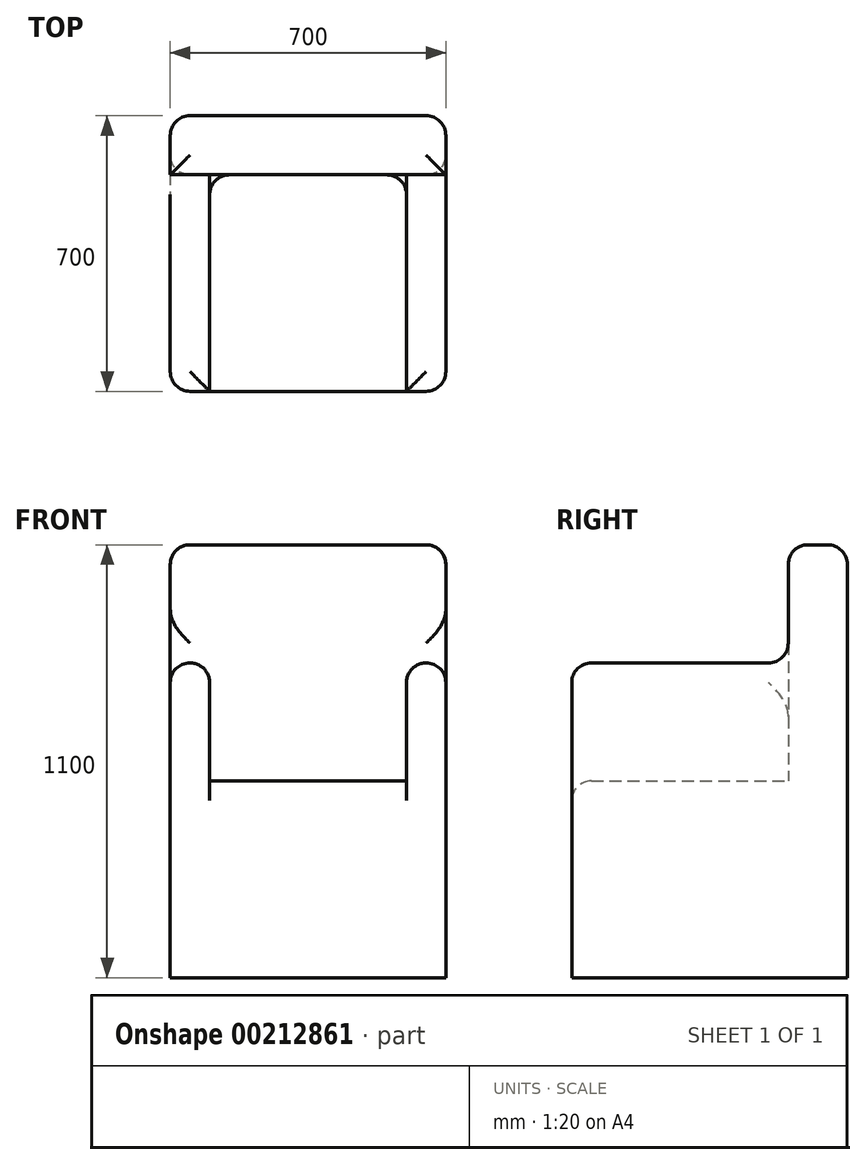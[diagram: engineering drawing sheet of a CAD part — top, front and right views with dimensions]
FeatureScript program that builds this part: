
annotation { "Feature Type Name" : "Feature", "Feature Type Description" : "" }
export const myFeature = defineFeature(function(context is Context, id is Id, definition is map)
    precondition{}
    {
        {
            var Q0;
            Q0=qCreatedBy(makeId("Top.planeOp"),FACE);
            var sketch = newSketch(context, id + "F0", { "sketchPlane" : qUnion([Q0])});
            skLineSegment(sketch, "E0.bottom", {"start": v(0, 0) * mm, "end": v(700, 0) * mm});
            skLineSegment(sketch, "E0.top", {"start": v(0, 700) * mm, "end": v(700, 700) * mm});
            skLineSegment(sketch, "E0.left", {"start": v(0, 0) * mm, "end": v(0, 700) * mm});
            skLineSegment(sketch, "E0.right", {"start": v(700, 0) * mm, "end": v(700, 700) * mm});
            skSolve(sketch);
        }
        {
            var Q0;
            Q0 = qSketchRegion(id + "F0", true);
            extrude(context, id + "F1", {"entities" : qUnion([Q0]), "depth" : 500 * mm});
        }
        {
            var Q0;
            Q0=makeQuery(id+"F1.opExtrude","CAP_FACE",FACE,{"disambiguationData":[OSD([sQuery(id+"F0.wireOp",EDGE,"E0.bottom"),sQuery(id+"F0.wireOp",EDGE,"E0.top"),sQuery(id+"F0.wireOp",EDGE,"E0.left"),sQuery(id+"F0.wireOp",EDGE,"E0.right")])],"isStart":false});
            var sketch = newSketch(context, id + "F2", { "sketchPlane" : qUnion([Q0])});
            skLineSegment(sketch, "E1", {"start": v(0, 0) * mm, "end": v(0, 700) * mm});
            skLineSegment(sketch, "E2", {"start": v(0, 700) * mm, "end": v(700, 700) * mm});
            skLineSegment(sketch, "E3", {"start": v(700, 700) * mm, "end": v(700, 0) * mm});
            skLineSegment(sketch, "E4", {"start": v(700, 0) * mm, "end": v(600, 0) * mm});
            skLineSegment(sketch, "E5", {"start": v(600, 0) * mm, "end": v(600, 550) * mm});
            skLineSegment(sketch, "E6", {"start": v(600, 550) * mm, "end": v(350, 550) * mm});
            skPoint(sketch, "E6.endSnap0", {"position": v(350, 700) * mm});
            skLineSegment(sketch, "E7", {"start": v(350, 700) * mm, "end": v(350, 438.14) * mm, "construction": true});
            skLineSegment(sketch, "E8.MirrorCS", {"start": v(100, 550) * mm, "end": v(350, 550) * mm});
            skLineSegment(sketch, "E9.MirrorCS", {"start": v(100, 0) * mm, "end": v(100, 550) * mm});
            skLineSegment(sketch, "E10.MirrorCS", {"start": v(0, 0) * mm, "end": v(100, 0) * mm});
            skSolve(sketch);
        }
        {
            var Q0;
            Q0 = qSketchRegion(id + "F2", true);
            extrude(context, id + "F3", {"entities" : qUnion([Q0]), "operationType" : NewBodyOperationType.ADD, "depth" : 300 * mm});
        }
        {
            var Q0;
            Q0=makeQuery(id+"F3.opExtrude","CAP_EDGE",EDGE,{"disambiguationData":[OSD([sQuery(id+"F2.wireOp",EDGE,"E6"),sQuery(id+"F2.wireOp",EDGE,"E8.MirrorCS")])],"isStart":true});
            var Q1;
            Q1=makeQuery(id+"F3.opExtrude","CAP_EDGE",EDGE,{"disambiguationData":[OSD([sQuery(id+"F2.wireOp",EDGE,"E5")])],"isStart":true});
            var Q2;
            Q2=makeQuery(id+"F1.opExtrude","CAP_EDGE",EDGE,{"disambiguationData":[OSD([sQuery(id+"F0.wireOp",EDGE,"E0.bottom")])],"isStart":false});
            var Q3;
            Q3=makeQuery(id+"F3.opExtrude","CAP_EDGE",EDGE,{"disambiguationData":[OSD([sQuery(id+"F2.wireOp",EDGE,"E9.MirrorCS")])],"isStart":true});
            var Q4;
            Q4=makeQuery(id+"F3.boolean.opBoolean","MERGE",EDGE,{"derivedFrom":[makeQuery(id+"F1.opExtrude","SWEPT_EDGE",EDGE,{"disambiguationData":[OSD([sQuery(id+"F0.wireOp",EDGE,"E0.bottom"),sQuery(id+"F0.wireOp",EDGE,"E0.right")])]}),makeQuery(id+"F3.opExtrude","SWEPT_EDGE",EDGE,{"disambiguationData":[OSD([sQuery(id+"F2.wireOp",EDGE,"E3"),sQuery(id+"F2.wireOp",EDGE,"E4")])]})]});
            var Q5;
            Q5=makeQuery(id+"F3.boolean.opBoolean","MERGE",EDGE,{"derivedFrom":[makeQuery(id+"F1.opExtrude","SWEPT_EDGE",EDGE,{"disambiguationData":[OSD([sQuery(id+"F0.wireOp",EDGE,"E0.bottom"),sQuery(id+"F0.wireOp",EDGE,"E0.left")])]}),makeQuery(id+"F3.opExtrude","SWEPT_EDGE",EDGE,{"disambiguationData":[OSD([sQuery(id+"F2.wireOp",EDGE,"E1"),sQuery(id+"F2.wireOp",EDGE,"E10.MirrorCS")])]})]});
            fillet(context, id + "F4", {"entities" : qUnion([Q0, Q1, Q2, Q3, Q4, Q5]), "radius" : 50 * mm, "tangentPropagation" : true, "allowEdgeOverflow" : false});
        }
        {
            var Q0;
            Q0=makeQuery(id+"F3.opExtrude","CAP_FACE",FACE,{"disambiguationData":[OSD([sQuery(id+"F2.wireOp",EDGE,"E1"),sQuery(id+"F2.wireOp",EDGE,"E2"),sQuery(id+"F2.wireOp",EDGE,"E3"),sQuery(id+"F2.wireOp",EDGE,"E4"),sQuery(id+"F2.wireOp",EDGE,"E5"),sQuery(id+"F2.wireOp",EDGE,"E6"),sQuery(id+"F2.wireOp",EDGE,"E8.MirrorCS"),sQuery(id+"F2.wireOp",EDGE,"E9.MirrorCS"),sQuery(id+"F2.wireOp",EDGE,"E10.MirrorCS")])],"isStart":false});
            var sketch = newSketch(context, id + "F5", { "sketchPlane" : qUnion([Q0])});
            skLineSegment(sketch, "E11.bottom", {"start": v(0, 700) * mm, "end": v(700, 700) * mm});
            skLineSegment(sketch, "E11.top", {"start": v(0, 550) * mm, "end": v(700, 550) * mm});
            skLineSegment(sketch, "E11.left", {"start": v(0, 700) * mm, "end": v(0, 550) * mm});
            skLineSegment(sketch, "E11.right", {"start": v(700, 700) * mm, "end": v(700, 550) * mm});
            skSolve(sketch);
        }
        {
            var Q0;
            Q0 = qSketchRegion(id + "F5", true);
            extrude(context, id + "F6", {"entities" : qUnion([Q0]), "operationType" : NewBodyOperationType.ADD, "depth" : 300 * mm});
        }
        {
            var Q0;
            Q0=makeQuery(id+"F6.opExtrude","CAP_FACE",FACE,{"disambiguationData":[OSD([sQuery(id+"F5.wireOp",EDGE,"E11.bottom"),sQuery(id+"F5.wireOp",EDGE,"E11.top"),sQuery(id+"F5.wireOp",EDGE,"E11.left"),sQuery(id+"F5.wireOp",EDGE,"E11.right")])],"isStart":false});
            var Q1;
            {var subQ0=sQuery(id+"F2.wireOp",EDGE,"E9.MirrorCS");var subQ1=sQuery(id+"F2.wireOp",EDGE,"E8.MirrorCS");var subQ2=sQuery(id+"F2.wireOp",EDGE,"E6");var subQ3=sQuery(id+"F2.wireOp",EDGE,"E1");var subQ4=sQuery(id+"F0.wireOp",EDGE,"E0.left");var subQ5=sQuery(id+"F2.wireOp",EDGE,"E10.MirrorCS");Q1=makeQuery(id+"F6.boolean.opBoolean","SPLIT",FACE,{"disambiguationData":[TD([makeQuery(id+"F1.opExtrude","SWEPT_FACE",FACE,{"disambiguationData":[OSD([subQ4])]})])],"derivedFrom":makeQuery(id+"F3.opExtrude","CAP_FACE",FACE,{"disambiguationData":[OSD([subQ3,sQuery(id+"F2.wireOp",EDGE,"E2"),sQuery(id+"F2.wireOp",EDGE,"E3"),sQuery(id+"F2.wireOp",EDGE,"E4"),sQuery(id+"F2.wireOp",EDGE,"E5"),subQ2,subQ1,subQ0,subQ5])],"isStart":false})});}
            var Q2;
            {var subQ0=sQuery(id+"F2.wireOp",EDGE,"E8.MirrorCS");var subQ1=sQuery(id+"F2.wireOp",EDGE,"E6");var subQ2=sQuery(id+"F2.wireOp",EDGE,"E4");var subQ3=sQuery(id+"F2.wireOp",EDGE,"E3");var subQ4=sQuery(id+"F0.wireOp",EDGE,"E0.right");var subQ5=sQuery(id+"F2.wireOp",EDGE,"E5");Q2=makeQuery(id+"F6.boolean.opBoolean","SPLIT",FACE,{"disambiguationData":[TD([makeQuery(id+"F1.opExtrude","SWEPT_FACE",FACE,{"disambiguationData":[OSD([subQ4])]})])],"derivedFrom":makeQuery(id+"F3.opExtrude","CAP_FACE",FACE,{"disambiguationData":[OSD([sQuery(id+"F2.wireOp",EDGE,"E1"),sQuery(id+"F2.wireOp",EDGE,"E2"),subQ3,subQ2,subQ5,subQ1,subQ0,sQuery(id+"F2.wireOp",EDGE,"E9.MirrorCS"),sQuery(id+"F2.wireOp",EDGE,"E10.MirrorCS")])],"isStart":false})});}
            fillet(context, id + "F7", {"entities" : qUnion([Q0, Q1, Q2]), "radius" : 50 * mm, "tangentPropagation" : true, "allowEdgeOverflow" : false});
        }
        {
            var Q0;
            Q0=makeQuery(id+"F6.boolean.opBoolean","MERGE",EDGE,{"derivedFrom":[makeQuery(id+"F3.boolean.opBoolean","MERGE",EDGE,{"derivedFrom":[makeQuery(id+"F1.opExtrude","SWEPT_EDGE",EDGE,{"disambiguationData":[OSD([sQuery(id+"F0.wireOp",EDGE,"E0.top"),sQuery(id+"F0.wireOp",EDGE,"E0.right")])]}),makeQuery(id+"F3.opExtrude","SWEPT_EDGE",EDGE,{"disambiguationData":[OSD([sQuery(id+"F2.wireOp",EDGE,"E2"),sQuery(id+"F2.wireOp",EDGE,"E3")])]})]}),makeQuery(id+"F6.opExtrude","SWEPT_EDGE",EDGE,{"disambiguationData":[OSD([sQuery(id+"F5.wireOp",EDGE,"E11.bottom"),sQuery(id+"F5.wireOp",EDGE,"E11.right")])]})]});
            var Q1;
            Q1=makeQuery(id+"F6.boolean.opBoolean","MERGE",EDGE,{"derivedFrom":[makeQuery(id+"F3.boolean.opBoolean","MERGE",EDGE,{"derivedFrom":[makeQuery(id+"F1.opExtrude","SWEPT_EDGE",EDGE,{"disambiguationData":[OSD([sQuery(id+"F0.wireOp",EDGE,"E0.top"),sQuery(id+"F0.wireOp",EDGE,"E0.left")])]}),makeQuery(id+"F3.opExtrude","SWEPT_EDGE",EDGE,{"disambiguationData":[OSD([sQuery(id+"F2.wireOp",EDGE,"E1"),sQuery(id+"F2.wireOp",EDGE,"E2")])]})]}),makeQuery(id+"F6.opExtrude","SWEPT_EDGE",EDGE,{"disambiguationData":[OSD([sQuery(id+"F5.wireOp",EDGE,"E11.bottom"),sQuery(id+"F5.wireOp",EDGE,"E11.left")])]})]});
            fillet(context, id + "F8", {"entities" : qUnion([Q0, Q1]), "radius" : 50 * mm, "tangentPropagation" : true, "allowEdgeOverflow" : false});
        }
    });
